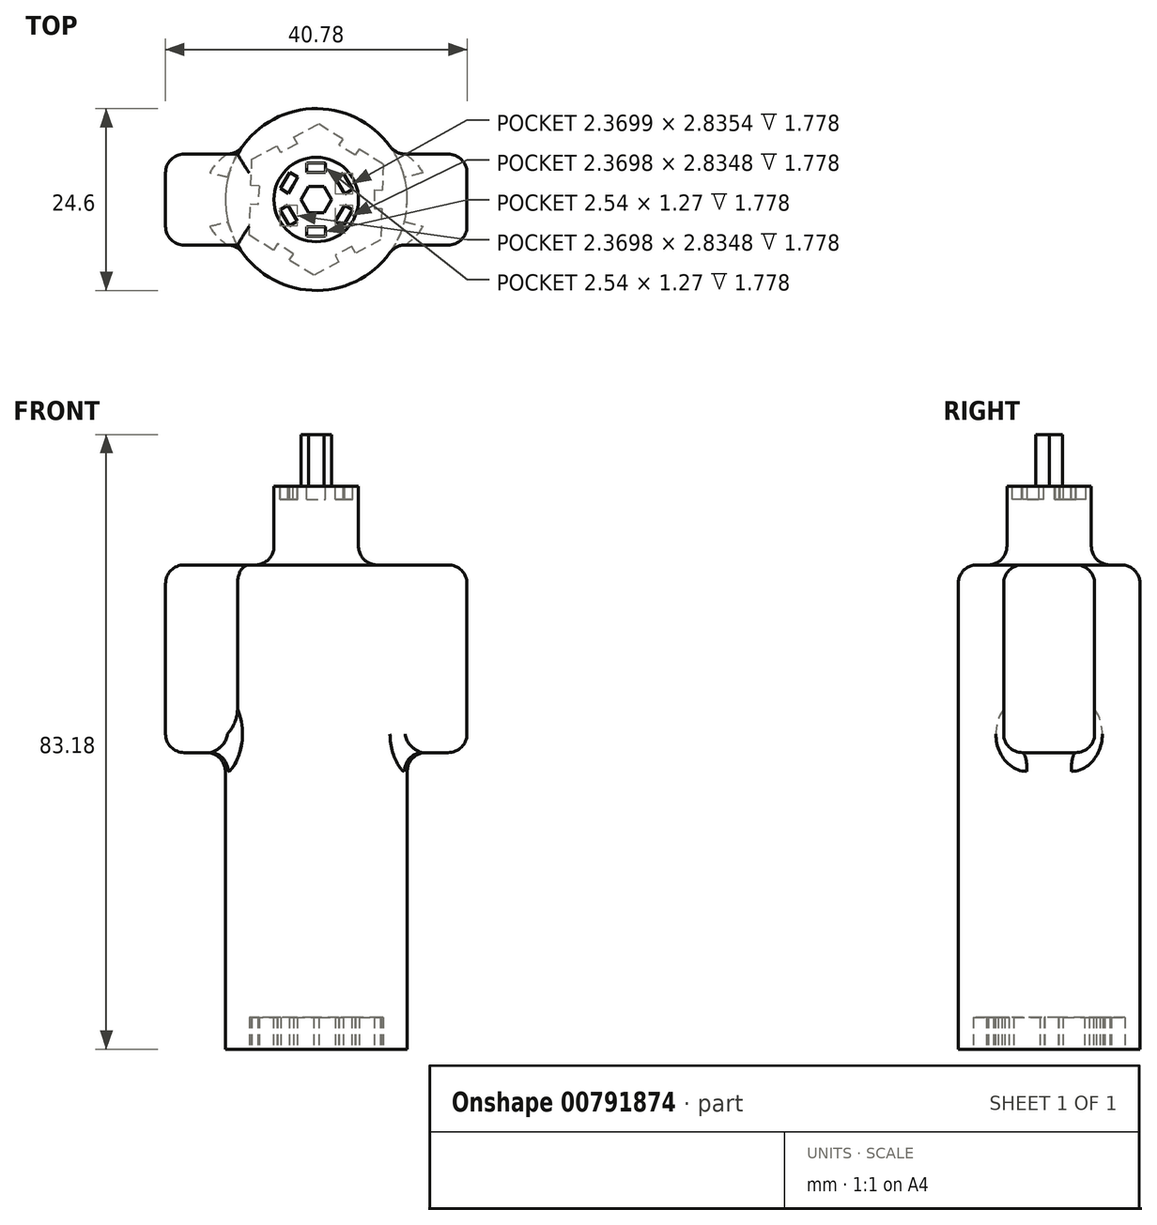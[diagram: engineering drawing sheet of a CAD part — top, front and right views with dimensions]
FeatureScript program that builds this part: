
annotation { "Feature Type Name" : "Feature", "Feature Type Description" : "" }
export const myFeature = defineFeature(function(context is Context, id is Id, definition is map)
    precondition{}
    {
        {
            var Q0;
            Q0=qCreatedBy(makeId("Top.planeOp"),FACE);
            var sketch = newSketch(context, id + "F0", { "sketchPlane" : qUnion([Q0])});
            skCircle(sketch, "E0.cCircle", {"center": v(0, 0) * mm, "radius": 8.9 * mm, "construction": true});
            skLineSegment(sketch, "E0.0", {"start": v(0.36, 10.26) * mm, "end": v(3.63, 8.21) * mm});
            skLineSegment(sketch, "E0.1", {"start": v(9.06, 4.82) * mm, "end": v(8.94, 1.27) * mm});
            skLineSegment(sketch, "E0.2", {"start": v(8.7, -5.44) * mm, "end": v(5.3, -7.25) * mm});
            skLineSegment(sketch, "E0.3", {"start": v(-0.36, -10.26) * mm, "end": v(-3.63, -8.21) * mm});
            skLineSegment(sketch, "E0.4", {"start": v(-9.06, -4.82) * mm, "end": v(-8.92, -0.61) * mm});
            skLineSegment(sketch, "E0.5", {"start": v(-8.7, 5.44) * mm, "end": v(-5.3, 7.25) * mm});
            skPoint(sketch, "E0.0.midPoint", {"position": v(4.71, 7.54) * mm});
            skLineSegment(sketch, "E1", {"start": v(0.36, 10.26) * mm, "end": v(-0.36, -10.26) * mm});
            skLineSegment(sketch, "E2", {"start": v(-9.06, -4.82) * mm, "end": v(9.06, 4.82) * mm});
            skLineSegment(sketch, "E3", {"start": v(-8.7, 5.44) * mm, "end": v(8.7, -5.44) * mm});
            skLineSegment(sketch, "E4", {"start": v(-3.05, 8.45) * mm, "end": v(-2.57, 7.55) * mm});
            skLineSegment(sketch, "E5", {"start": v(-2.57, 7.55) * mm, "end": v(-4.82, 6.36) * mm});
            skLineSegment(sketch, "E6", {"start": v(-4.82, 6.36) * mm, "end": v(-5.3, 7.25) * mm});
            skLineSegment(sketch, "E7.trimOffspring", {"start": v(-3.05, 8.45) * mm, "end": v(0.36, 10.26) * mm});
            skLineSegment(sketch, "E8.MirrorCS", {"start": v(2.57, -7.55) * mm, "end": v(3.05, -8.45) * mm});
            skLineSegment(sketch, "E9.MirrorCS", {"start": v(4.82, -6.36) * mm, "end": v(2.57, -7.55) * mm});
            skLineSegment(sketch, "E10.MirrorCS", {"start": v(5.3, -7.25) * mm, "end": v(4.82, -6.36) * mm});
            skLineSegment(sketch, "E11", {"start": v(5.79, 6.87) * mm, "end": v(5.25, 6) * mm});
            skLineSegment(sketch, "E12", {"start": v(5.25, 6) * mm, "end": v(3.1, 7.35) * mm});
            skLineSegment(sketch, "E13", {"start": v(3.1, 7.35) * mm, "end": v(3.63, 8.21) * mm});
            skLineSegment(sketch, "E14", {"start": v(7.84, 1.3) * mm, "end": v(7.84, -1.24) * mm});
            skLineSegment(sketch, "E15", {"start": v(7.84, -1.24) * mm, "end": v(8.85, -1.24) * mm});
            skLineSegment(sketch, "E16", {"start": v(7.84, 1.3) * mm, "end": v(8.94, 1.27) * mm});
            skLineSegment(sketch, "E17.MirrorCS", {"start": v(-3.1, -7.35) * mm, "end": v(-5.25, -6) * mm});
            skLineSegment(sketch, "E18.MirrorCS", {"start": v(-5.25, -6) * mm, "end": v(-5.79, -6.87) * mm});
            skLineSegment(sketch, "E19.MirrorCS", {"start": v(-3.63, -8.21) * mm, "end": v(-3.1, -7.35) * mm});
            skLineSegment(sketch, "E20.MirrorCS", {"start": v(-7.73, 1.85) * mm, "end": v(-8.83, 1.9) * mm});
            skLineSegment(sketch, "E21.MirrorCS", {"start": v(-7.73, 1.85) * mm, "end": v(-7.9, -0.68) * mm});
            skLineSegment(sketch, "E22.MirrorCS", {"start": v(-7.9, -0.68) * mm, "end": v(-8.92, -0.61) * mm});
            skLineSegment(sketch, "E23.trimOffspring", {"start": v(5.79, 6.87) * mm, "end": v(9.06, 4.82) * mm});
            skPoint(sketch, "E24.start.orphan", {"position": v(8.9, 0) * mm});
            skLineSegment(sketch, "E25.trimOffspring", {"start": v(8.85, -1.24) * mm, "end": v(8.7, -5.44) * mm});
            skLineSegment(sketch, "E26.trimOffspring", {"start": v(3.05, -8.45) * mm, "end": v(-0.36, -10.26) * mm});
            skLineSegment(sketch, "E27.trimOffspring", {"start": v(-5.79, -6.87) * mm, "end": v(-9.06, -4.82) * mm});
            skLineSegment(sketch, "E28.trimOffspring", {"start": v(-8.83, 1.9) * mm, "end": v(-8.7, 5.44) * mm});
            skPoint(sketch, "E29.start.orphan", {"position": v(-4.17, 7.85) * mm});
            skLineSegment(sketch, "E30", {"start": v(-5.3, 7.25) * mm, "end": v(-3.05, 8.45) * mm});
            skLineSegment(sketch, "E31", {"start": v(3.63, 8.21) * mm, "end": v(5.79, 6.87) * mm});
            skLineSegment(sketch, "E32", {"start": v(8.94, 1.27) * mm, "end": v(8.85, -1.24) * mm});
            skLineSegment(sketch, "E33", {"start": v(5.3, -7.25) * mm, "end": v(3.05, -8.45) * mm});
            skLineSegment(sketch, "E34", {"start": v(-5.79, -6.87) * mm, "end": v(-3.63, -8.21) * mm});
            skLineSegment(sketch, "E35", {"start": v(-8.83, 1.9) * mm, "end": v(-8.92, -0.61) * mm});
            skCircle(sketch, "E36", {"center": v(0, 0) * mm, "radius": 12.3 * mm});
            skSolve(sketch);
        }
        {
            var Q0;
            Q0=makeQuery(id+"F0.imprint","IMPRINT",FACE,{"disambiguationData":[TD([[makeQuery(id+"F0.imprint","IMPRINT",EDGE,{"derivedFrom":sQuery(id+"F0.wireOp",EDGE,"E0.0")}),1.0]])]});
            var Q1;
            Q1=makeQuery(id+"F0.imprint","IMPRINT",FACE,{"disambiguationData":[TD([[makeQuery(id+"F0.imprint","IMPRINT",EDGE,{"derivedFrom":sQuery(id+"F0.wireOp",EDGE,"E4")}),-1.0]])]});
            var Q2;
            Q2=makeQuery(id+"F0.imprint","IMPRINT",FACE,{"disambiguationData":[TD([[makeQuery(id+"F0.imprint","IMPRINT",EDGE,{"derivedFrom":sQuery(id+"F0.wireOp",EDGE,"E20.MirrorCS")}),1.0]])]});
            var Q3;
            Q3=makeQuery(id+"F0.imprint","IMPRINT",FACE,{"disambiguationData":[TD([[makeQuery(id+"F0.imprint","IMPRINT",EDGE,{"derivedFrom":sQuery(id+"F0.wireOp",EDGE,"E17.MirrorCS")}),1.0]])]});
            var Q4;
            Q4=makeQuery(id+"F0.imprint","IMPRINT",FACE,{"disambiguationData":[TD([[makeQuery(id+"F0.imprint","IMPRINT",EDGE,{"derivedFrom":sQuery(id+"F0.wireOp",EDGE,"E11")}),-1.0]])]});
            var Q5;
            {var subQ4=sQuery(id+"F0.wireOp",EDGE,"E0.0");Q5=makeQuery(id+"F0.imprint","IMPRINT",FACE,{"disambiguationData":[TD([[makeQuery(id+"F0.imprint","IMPRINT",EDGE,{"derivedFrom":subQ4}),-1.0]])]});}
            var Q6;
            {var subQ1=sQuery(id+"F0.wireOp",EDGE,"E0.5");Q6=makeQuery(id+"F0.imprint","IMPRINT",FACE,{"disambiguationData":[TD([[makeQuery(id+"F0.imprint","IMPRINT",EDGE,{"derivedFrom":subQ1}),-1.0]])]});}
            var Q7;
            {var subQ4=sQuery(id+"F0.wireOp",EDGE,"E0.4");Q7=makeQuery(id+"F0.imprint","IMPRINT",FACE,{"disambiguationData":[TD([[makeQuery(id+"F0.imprint","IMPRINT",EDGE,{"derivedFrom":subQ4}),-1.0]])]});}
            var Q8;
            {var subQ4=sQuery(id+"F0.wireOp",EDGE,"E0.1");Q8=makeQuery(id+"F0.imprint","IMPRINT",FACE,{"disambiguationData":[TD([[makeQuery(id+"F0.imprint","IMPRINT",EDGE,{"derivedFrom":subQ4}),-1.0]])]});}
            var Q9;
            Q9=makeQuery(id+"F0.imprint","IMPRINT",FACE,{"disambiguationData":[TD([[makeQuery(id+"F0.imprint","IMPRINT",EDGE,{"derivedFrom":sQuery(id+"F0.wireOp",EDGE,"E14")}),1.0]])]});
            var Q10;
            {var subQ1=sQuery(id+"F0.wireOp",EDGE,"E0.2");Q10=makeQuery(id+"F0.imprint","IMPRINT",FACE,{"disambiguationData":[TD([[makeQuery(id+"F0.imprint","IMPRINT",EDGE,{"derivedFrom":subQ1}),-1.0]])]});}
            var Q11;
            {var subQ0=sQuery(id+"F0.wireOp",EDGE,"E0.3");Q11=makeQuery(id+"F0.imprint","IMPRINT",FACE,{"disambiguationData":[TD([[makeQuery(id+"F0.imprint","IMPRINT",EDGE,{"derivedFrom":subQ0}),-1.0]])]});}
            var Q12;
            Q12=makeQuery(id+"F0.imprint","IMPRINT",FACE,{"disambiguationData":[TD([[makeQuery(id+"F0.imprint","IMPRINT",EDGE,{"derivedFrom":sQuery(id+"F0.wireOp",EDGE,"E8.MirrorCS")}),1.0]])]});
            extrude(context, id + "F1", {"entities" : qUnion([Q0, Q1, Q2, Q3, Q4, Q5, Q6, Q7, Q8, Q9, Q10, Q11, Q12]), "depth" : 76.2 * mm, "offsetDistance" : 25.4 * mm});
        }
        {
            var Q0;
            {var subQ1=sQuery(id+"F0.wireOp",EDGE,"E0.5");Q0=makeQuery(id+"F0.imprint","IMPRINT",FACE,{"disambiguationData":[TD([[makeQuery(id+"F0.imprint","IMPRINT",EDGE,{"derivedFrom":subQ1}),-1.0]])]});}
            var Q1;
            {var subQ4=sQuery(id+"F0.wireOp",EDGE,"E0.4");Q1=makeQuery(id+"F0.imprint","IMPRINT",FACE,{"disambiguationData":[TD([[makeQuery(id+"F0.imprint","IMPRINT",EDGE,{"derivedFrom":subQ4}),-1.0]])]});}
            var Q2;
            {var subQ0=sQuery(id+"F0.wireOp",EDGE,"E0.3");Q2=makeQuery(id+"F0.imprint","IMPRINT",FACE,{"disambiguationData":[TD([[makeQuery(id+"F0.imprint","IMPRINT",EDGE,{"derivedFrom":subQ0}),-1.0]])]});}
            var Q3;
            {var subQ1=sQuery(id+"F0.wireOp",EDGE,"E0.2");Q3=makeQuery(id+"F0.imprint","IMPRINT",FACE,{"disambiguationData":[TD([[makeQuery(id+"F0.imprint","IMPRINT",EDGE,{"derivedFrom":subQ1}),-1.0]])]});}
            var Q4;
            {var subQ4=sQuery(id+"F0.wireOp",EDGE,"E0.1");Q4=makeQuery(id+"F0.imprint","IMPRINT",FACE,{"disambiguationData":[TD([[makeQuery(id+"F0.imprint","IMPRINT",EDGE,{"derivedFrom":subQ4}),-1.0]])]});}
            var Q5;
            {var subQ4=sQuery(id+"F0.wireOp",EDGE,"E0.0");Q5=makeQuery(id+"F0.imprint","IMPRINT",FACE,{"disambiguationData":[TD([[makeQuery(id+"F0.imprint","IMPRINT",EDGE,{"derivedFrom":subQ4}),-1.0]])]});}
            extrude(context, id + "F2", {"entities" : qUnion([Q0, Q1, Q2, Q3, Q4, Q5]), "operationType" : NewBodyOperationType.REMOVE, "depth" : 4.32 * mm, "offsetDistance" : 25.4 * mm});
        }
        {
            var Q0;
            Q0=makeQuery(id+"F1.opExtrude","CAP_FACE",FACE,{"disambiguationData":[OSD([sQuery(id+"F0.wireOp",EDGE,"E36")])],"isStart":false});
            var sketch = newSketch(context, id + "F3", { "sketchPlane" : qUnion([Q0])});
            skCircle(sketch, "E37.cCircle", {"center": v(0, 0) * mm, "radius": 1.78 * mm, "construction": true});
            skLineSegment(sketch, "E37.0", {"start": v(-1.03, 1.78) * mm, "end": v(1.03, 1.78) * mm});
            skLineSegment(sketch, "E37.1", {"start": v(1.03, 1.78) * mm, "end": v(2.05, 0) * mm});
            skLineSegment(sketch, "E37.2", {"start": v(2.05, 0) * mm, "end": v(1.03, -1.78) * mm});
            skLineSegment(sketch, "E37.3", {"start": v(1.03, -1.78) * mm, "end": v(-1.03, -1.78) * mm});
            skLineSegment(sketch, "E37.4", {"start": v(-1.03, -1.78) * mm, "end": v(-2.05, 0) * mm});
            skLineSegment(sketch, "E37.5", {"start": v(-2.05, 0) * mm, "end": v(-1.03, 1.78) * mm});
            skPoint(sketch, "E37.0.midPoint", {"position": v(0, 1.78) * mm});
            skLineSegment(sketch, "E38.bottom", {"start": v(-1.27, 4.95) * mm, "end": v(1.27, 4.95) * mm});
            skLineSegment(sketch, "E38.top", {"start": v(-1.27, 3.68) * mm, "end": v(1.27, 3.68) * mm});
            skLineSegment(sketch, "E38.left", {"start": v(-1.27, 4.95) * mm, "end": v(-1.27, 3.68) * mm});
            skLineSegment(sketch, "E38.right", {"start": v(1.27, 4.95) * mm, "end": v(1.27, 3.68) * mm});
            skLineSegment(sketch, "E39", {"start": v(0, 4.95) * mm, "end": v(0, 0) * mm});
            skPoint(sketch, "E40.endSnap0", {"position": v(0, -1.78) * mm});
            skLineSegment(sketch, "E41", {"start": v(3.19, 1.84) * mm, "end": v(2.55, 2.94) * mm});
            skLineSegment(sketch, "E42", {"start": v(3.19, 1.84) * mm, "end": v(3.82, 0.74) * mm});
            skLineSegment(sketch, "E43", {"start": v(0, -3.68) * mm, "end": v(1.27, -3.68) * mm});
            skLineSegment(sketch, "E44", {"start": v(0, -3.68) * mm, "end": v(-1.27, -3.68) * mm});
            skLineSegment(sketch, "E45", {"start": v(-3.19, -1.84) * mm, "end": v(-2.55, -2.94) * mm});
            skLineSegment(sketch, "E46", {"start": v(-3.19, -1.84) * mm, "end": v(-3.82, -0.74) * mm});
            skLineSegment(sketch, "E47", {"start": v(-3.12, 1.93) * mm, "end": v(-2.48, 3.03) * mm});
            skLineSegment(sketch, "E48", {"start": v(-2.48, 3.03) * mm, "end": v(-3.58, 3.66) * mm});
            skLineSegment(sketch, "E49", {"start": v(2.55, 2.94) * mm, "end": v(2.56, 2.94) * mm});
            skLineSegment(sketch, "E50", {"start": v(3.82, 0.74) * mm, "end": v(4.92, 1.38) * mm});
            skLineSegment(sketch, "E51", {"start": v(1.27, -3.68) * mm, "end": v(1.27, -4.95) * mm});
            skLineSegment(sketch, "E52", {"start": v(-1.27, -3.68) * mm, "end": v(-1.27, -4.95) * mm});
            skLineSegment(sketch, "E53", {"start": v(-2.55, -2.94) * mm, "end": v(-3.65, -3.58) * mm});
            skPoint(sketch, "E54.endSnap0", {"position": v(-3.5, -1.3) * mm});
            skLineSegment(sketch, "E55", {"start": v(-3.12, 1.93) * mm, "end": v(-3.78, 0.85) * mm});
            skLineSegment(sketch, "E56", {"start": v(-3.78, 0.85) * mm, "end": v(-4.86, 1.51) * mm});
            skLineSegment(sketch, "E57", {"start": v(-4.86, 1.51) * mm, "end": v(-3.58, 3.66) * mm});
            skLineSegment(sketch, "E58", {"start": v(2.56, 2.94) * mm, "end": v(3.65, 3.58) * mm});
            skLineSegment(sketch, "E59", {"start": v(3.65, 3.58) * mm, "end": v(4.92, 1.38) * mm});
            skLineSegment(sketch, "E60", {"start": v(1.27, -4.95) * mm, "end": v(-1.27, -4.95) * mm});
            skLineSegment(sketch, "E61", {"start": v(-3.82, -0.74) * mm, "end": v(-4.92, -1.38) * mm});
            skLineSegment(sketch, "E62", {"start": v(-4.92, -1.38) * mm, "end": v(-3.65, -3.58) * mm});
            skLineSegment(sketch, "E63", {"start": v(-4.22, 2.59) * mm, "end": v(0, 0) * mm});
            skLineSegment(sketch, "E64", {"start": v(-4.29, -2.48) * mm, "end": v(0, 0) * mm});
            skLineSegment(sketch, "E65", {"start": v(4.29, 2.48) * mm, "end": v(0, 0) * mm});
            skLineSegment(sketch, "E66", {"start": v(0, -4.95) * mm, "end": v(0, 0) * mm});
            skLineSegment(sketch, "E67", {"start": v(-1.27, -4.95) * mm, "end": v(1.27, -4.95) * mm});
            skLineSegment(sketch, "E68", {"start": v(3.19, -1.84) * mm, "end": v(3.82, -0.74) * mm});
            skLineSegment(sketch, "E69", {"start": v(3.19, -1.84) * mm, "end": v(2.55, -2.94) * mm});
            skLineSegment(sketch, "E70", {"start": v(2.55, -2.94) * mm, "end": v(3.65, -3.58) * mm});
            skLineSegment(sketch, "E71", {"start": v(3.82, -0.74) * mm, "end": v(4.92, -1.38) * mm});
            skLineSegment(sketch, "E72", {"start": v(4.92, -1.38) * mm, "end": v(3.65, -3.58) * mm});
            skLineSegment(sketch, "E73", {"start": v(4.29, -2.48) * mm, "end": v(0, 0) * mm});
            skCircle(sketch, "E74", {"center": v(0, 0) * mm, "radius": 5.72 * mm});
            skCircle(sketch, "E75", {"center": v(0, 0) * mm, "radius": 12.63 * mm});
            skSolve(sketch);
        }
        {
            var Q0;
            {var subQ0=sQuery(id+"F3.wireOp",EDGE,"E37.1");var subQ1=sQuery(id+"F3.wireOp",EDGE,"E37.0");var subQ2=makeQuery(id+"F3.imprint","INTERSECT",VERTEX,{"derivedFrom":[subQ1,subQ0]});Q0=makeQuery(id+"F3.imprint","IMPRINT",FACE,{"disambiguationData":[TD([[makeQuery(id+"F3.imprint","IMPRINT",EDGE,{"disambiguationData":[TD([[subQ2,1.0]])],"derivedFrom":subQ1}),-1.0]])]});}
            var Q1;
            {var subQ0=sQuery(id+"F3.wireOp",EDGE,"E37.5");var subQ1=sQuery(id+"F3.wireOp",EDGE,"E37.0");var subQ2=makeQuery(id+"F3.imprint","INTERSECT",VERTEX,{"derivedFrom":[subQ1,subQ0]});Q1=makeQuery(id+"F3.imprint","IMPRINT",FACE,{"disambiguationData":[TD([[makeQuery(id+"F3.imprint","IMPRINT",EDGE,{"disambiguationData":[TD([[subQ2,-1.0]])],"derivedFrom":subQ1}),-1.0]])]});}
            var Q2;
            {var subQ0=sQuery(id+"F3.wireOp",EDGE,"E37.5");var subQ1=sQuery(id+"F3.wireOp",EDGE,"E37.4");var subQ2=makeQuery(id+"F3.imprint","INTERSECT",VERTEX,{"derivedFrom":[subQ1,subQ0]});Q2=makeQuery(id+"F3.imprint","IMPRINT",FACE,{"disambiguationData":[TD([[makeQuery(id+"F3.imprint","IMPRINT",EDGE,{"disambiguationData":[TD([[subQ2,1.0]])],"derivedFrom":subQ1}),-1.0]])]});}
            var Q3;
            {var subQ0=sQuery(id+"F3.wireOp",EDGE,"E37.4");var subQ1=sQuery(id+"F3.wireOp",EDGE,"E37.3");var subQ2=makeQuery(id+"F3.imprint","INTERSECT",VERTEX,{"derivedFrom":[subQ1,subQ0]});Q3=makeQuery(id+"F3.imprint","IMPRINT",FACE,{"disambiguationData":[TD([[makeQuery(id+"F3.imprint","IMPRINT",EDGE,{"disambiguationData":[TD([[subQ2,1.0]])],"derivedFrom":subQ1}),-1.0]])]});}
            var Q4;
            {var subQ0=sQuery(id+"F3.wireOp",EDGE,"E37.3");var subQ1=sQuery(id+"F3.wireOp",EDGE,"E37.2");var subQ2=makeQuery(id+"F3.imprint","INTERSECT",VERTEX,{"derivedFrom":[subQ1,subQ0]});Q4=makeQuery(id+"F3.imprint","IMPRINT",FACE,{"disambiguationData":[TD([[makeQuery(id+"F3.imprint","IMPRINT",EDGE,{"disambiguationData":[TD([[subQ2,1.0]])],"derivedFrom":subQ1}),-1.0]])]});}
            var Q5;
            {var subQ0=sQuery(id+"F3.wireOp",EDGE,"E37.2");var subQ1=sQuery(id+"F3.wireOp",EDGE,"E37.1");var subQ2=makeQuery(id+"F3.imprint","INTERSECT",VERTEX,{"derivedFrom":[subQ1,subQ0]});Q5=makeQuery(id+"F3.imprint","IMPRINT",FACE,{"disambiguationData":[TD([[makeQuery(id+"F3.imprint","IMPRINT",EDGE,{"disambiguationData":[TD([[subQ2,1.0]])],"derivedFrom":subQ1}),-1.0]])]});}
            extrude(context, id + "F4", {"entities" : qUnion([Q0, Q1, Q2, Q3, Q4, Q5]), "operationType" : NewBodyOperationType.ADD, "depth" : 6.98 * mm, "offsetDistance" : 25.4 * mm});
        }
        {
            var Q0;
            {var subQ0=sQuery(id+"F3.wireOp",EDGE,"E38.left");Q0=makeQuery(id+"F3.imprint","IMPRINT",FACE,{"disambiguationData":[TD([[makeQuery(id+"F3.imprint","IMPRINT",EDGE,{"derivedFrom":subQ0}),1.0]])]});}
            var Q1;
            {var subQ0=sQuery(id+"F3.wireOp",EDGE,"E38.right");Q1=makeQuery(id+"F3.imprint","IMPRINT",FACE,{"disambiguationData":[TD([[makeQuery(id+"F3.imprint","IMPRINT",EDGE,{"derivedFrom":subQ0}),-1.0]])]});}
            var Q2;
            {var subQ4=sQuery(id+"F3.wireOp",EDGE,"E41");Q2=makeQuery(id+"F3.imprint","IMPRINT",FACE,{"disambiguationData":[TD([[makeQuery(id+"F3.imprint","IMPRINT",EDGE,{"derivedFrom":subQ4}),-1.0]])]});}
            var Q3;
            {var subQ0=sQuery(id+"F3.wireOp",EDGE,"E42");Q3=makeQuery(id+"F3.imprint","IMPRINT",FACE,{"disambiguationData":[TD([[makeQuery(id+"F3.imprint","IMPRINT",EDGE,{"derivedFrom":subQ0}),1.0]])]});}
            var Q4;
            {var subQ0=sQuery(id+"F3.wireOp",EDGE,"E68");Q4=makeQuery(id+"F3.imprint","IMPRINT",FACE,{"disambiguationData":[TD([[makeQuery(id+"F3.imprint","IMPRINT",EDGE,{"derivedFrom":subQ0}),-1.0]])]});}
            var Q5;
            {var subQ0=sQuery(id+"F3.wireOp",EDGE,"E69");Q5=makeQuery(id+"F3.imprint","IMPRINT",FACE,{"disambiguationData":[TD([[makeQuery(id+"F3.imprint","IMPRINT",EDGE,{"derivedFrom":subQ0}),1.0]])]});}
            var Q6;
            {var subQ0=sQuery(id+"F3.wireOp",EDGE,"E43");Q6=makeQuery(id+"F3.imprint","IMPRINT",FACE,{"disambiguationData":[TD([[makeQuery(id+"F3.imprint","IMPRINT",EDGE,{"derivedFrom":subQ0}),-1.0]])]});}
            var Q7;
            {var subQ0=sQuery(id+"F3.wireOp",EDGE,"E44");Q7=makeQuery(id+"F3.imprint","IMPRINT",FACE,{"disambiguationData":[TD([[makeQuery(id+"F3.imprint","IMPRINT",EDGE,{"derivedFrom":subQ0}),1.0]])]});}
            var Q8;
            {var subQ0=sQuery(id+"F3.wireOp",EDGE,"E45");Q8=makeQuery(id+"F3.imprint","IMPRINT",FACE,{"disambiguationData":[TD([[makeQuery(id+"F3.imprint","IMPRINT",EDGE,{"derivedFrom":subQ0}),-1.0]])]});}
            var Q9;
            {var subQ0=sQuery(id+"F3.wireOp",EDGE,"E46");Q9=makeQuery(id+"F3.imprint","IMPRINT",FACE,{"disambiguationData":[TD([[makeQuery(id+"F3.imprint","IMPRINT",EDGE,{"derivedFrom":subQ0}),1.0]])]});}
            var Q10;
            {var subQ1=sQuery(id+"F3.wireOp",EDGE,"E47");Q10=makeQuery(id+"F3.imprint","IMPRINT",FACE,{"disambiguationData":[TD([[makeQuery(id+"F3.imprint","IMPRINT",EDGE,{"derivedFrom":subQ1}),1.0]])]});}
            var Q11;
            {var subQ3=sQuery(id+"F3.wireOp",EDGE,"E56");Q11=makeQuery(id+"F3.imprint","IMPRINT",FACE,{"disambiguationData":[TD([[makeQuery(id+"F3.imprint","IMPRINT",EDGE,{"derivedFrom":subQ3}),-1.0]])]});}
            extrude(context, id + "F5", {"entities" : qUnion([Q0, Q1, Q2, Q3, Q4, Q5, Q6, Q7, Q8, Q9, Q10, Q11]), "operationType" : NewBodyOperationType.REMOVE, "oppositeDirection" : true, "depth" : 1.78 * mm, "offsetDistance" : 25.4 * mm});
        }
        {
            var Q0;
            Q0=makeQuery(id+"F3.imprint","IMPRINT",FACE,{"disambiguationData":[TD([[makeQuery(id+"F3.imprint","IMPRINT",EDGE,{"derivedFrom":sQuery(id+"F3.wireOp",EDGE,"E74")}),-1.0]])]});
            extrude(context, id + "F6", {"entities" : qUnion([Q0]), "operationType" : NewBodyOperationType.REMOVE, "oppositeDirection" : true, "depth" : 10.67 * mm, "offsetDistance" : 25.4 * mm});
        }
        {
            var Q0;
            Q0=makeQuery(id+"F6.boolean.opBoolean","COPY",FACE,{"derivedFrom":makeQuery(id+"F6.opExtrude","CAP_FACE",FACE,{"disambiguationData":[OSD([sQuery(id+"F0.wireOp",EDGE,"E36"),sQuery(id+"F3.wireOp",EDGE,"E74")])],"isStart":false})});
            var sketch = newSketch(context, id + "F7", { "sketchPlane" : qUnion([Q0])});
            skLineSegment(sketch, "E76.bottom", {"start": v(-10.66, 6.15) * mm, "end": v(-20.39, 6.15) * mm});
            skLineSegment(sketch, "E76.top", {"start": v(-10.66, -6.15) * mm, "end": v(-20.39, -6.15) * mm});
            skLineSegment(sketch, "E76.left", {"start": v(-10.66, 6.15) * mm, "end": v(-10.66, -6.15) * mm});
            skLineSegment(sketch, "E76.right", {"start": v(-20.39, 6.15) * mm, "end": v(-20.39, -6.15) * mm});
            skLineSegment(sketch, "E77", {"start": v(0, 12.3) * mm, "end": v(0, -12.3) * mm});
            skLineSegment(sketch, "E78.MirrorCS", {"start": v(10.66, 6.15) * mm, "end": v(20.39, 6.15) * mm});
            skLineSegment(sketch, "E79.MirrorCS", {"start": v(20.39, 6.15) * mm, "end": v(20.39, -6.15) * mm});
            skLineSegment(sketch, "E80.MirrorCS", {"start": v(10.66, -6.15) * mm, "end": v(20.39, -6.15) * mm});
            skLineSegment(sketch, "E81.MirrorCS", {"start": v(10.66, 6.15) * mm, "end": v(10.66, -6.15) * mm});
            skPoint(sketch, "E82.MirrorCS.end.orphan", {"position": v(-20.39, 18.45) * mm});
            skPoint(sketch, "E82.MirrorCS.start.orphan", {"position": v(-20.39, 6.15) * mm});
            skLineSegment(sketch, "E83", {"start": v(0, 0) * mm, "end": v(-20.39, 0) * mm});
            skLineSegment(sketch, "E84", {"start": v(0, 0) * mm, "end": v(20.39, 0) * mm});
            skSolve(sketch);
        }
        {
            var Q0;
            {var subQ0=sQuery(id+"F7.wireOp",EDGE,"E76.bottom");Q0=makeQuery(id+"F7.imprint","IMPRINT",FACE,{"disambiguationData":[TD([[makeQuery(id+"F7.imprint","IMPRINT",EDGE,{"derivedFrom":subQ0}),1.0]])]});}
            var Q1;
            {var subQ0=sQuery(id+"F7.wireOp",EDGE,"E78.MirrorCS");Q1=makeQuery(id+"F7.imprint","IMPRINT",FACE,{"disambiguationData":[TD([[makeQuery(id+"F7.imprint","IMPRINT",EDGE,{"derivedFrom":subQ0}),-1.0]])]});}
            var Q2;
            {var subQ0=sQuery(id+"F7.wireOp",EDGE,"E76.top");Q2=makeQuery(id+"F7.imprint","IMPRINT",FACE,{"disambiguationData":[TD([[makeQuery(id+"F7.imprint","IMPRINT",EDGE,{"derivedFrom":subQ0}),-1.0]])]});}
            var Q3;
            {var subQ0=sQuery(id+"F7.wireOp",EDGE,"E80.MirrorCS");Q3=makeQuery(id+"F7.imprint","IMPRINT",FACE,{"disambiguationData":[TD([[makeQuery(id+"F7.imprint","IMPRINT",EDGE,{"derivedFrom":subQ0}),1.0]])]});}
            extrude(context, id + "F8", {"entities" : qUnion([Q0, Q1, Q2, Q3]), "operationType" : NewBodyOperationType.ADD, "oppositeDirection" : true, "depth" : 25.4 * mm, "offsetDistance" : 25.4 * mm});
        }
        {
            var Q0;
            Q0=makeQuery(id+"F8.opExtrude","SWEPT_FACE",FACE,{"disambiguationData":[OSD([sQuery(id+"F7.wireOp",EDGE,"E76.right")])]});
            var Q1;
            Q1=makeQuery(id+"F8.opExtrude","CAP_FACE",FACE,{"disambiguationData":[OSD([sQuery(id+"F0.wireOp",EDGE,"E36"),sQuery(id+"F7.wireOp",EDGE,"E76.bottom"),sQuery(id+"F7.wireOp",EDGE,"E76.top"),sQuery(id+"F7.wireOp",EDGE,"E76.right")])],"isStart":false});
            var Q2;
            Q2=makeQuery(id+"F8.opExtrude","CAP_EDGE",EDGE,{"disambiguationData":[OSD([sQuery(id+"F7.wireOp",EDGE,"E76.top")])],"isStart":true});
            var Q3;
            Q3=makeQuery(id+"F8.opExtrude","CAP_EDGE",EDGE,{"disambiguationData":[OSD([sQuery(id+"F7.wireOp",EDGE,"E76.bottom")])],"isStart":true});
            var Q4;
            {var subQ0=sQuery(id+"F0.wireOp",EDGE,"E36");Q4=makeQuery(id+"F8.boolean.opBoolean","MERGE",FACE,{"derivedFrom":[makeQuery(id+"F6.boolean.opBoolean","COPY",FACE,{"derivedFrom":makeQuery(id+"F6.opExtrude","CAP_FACE",FACE,{"disambiguationData":[OSD([subQ0,sQuery(id+"F3.wireOp",EDGE,"E74")])],"isStart":false})}),makeQuery(id+"F8.opExtrude","CAP_FACE",FACE,{"disambiguationData":[OSD([subQ0,sQuery(id+"F7.wireOp",EDGE,"E76.bottom"),sQuery(id+"F7.wireOp",EDGE,"E76.top"),sQuery(id+"F7.wireOp",EDGE,"E76.right")])],"isStart":true}),makeQuery(id+"F8.opExtrude","CAP_FACE",FACE,{"disambiguationData":[OSD([subQ0,sQuery(id+"F7.wireOp",EDGE,"E78.MirrorCS"),sQuery(id+"F7.wireOp",EDGE,"E79.MirrorCS"),sQuery(id+"F7.wireOp",EDGE,"E80.MirrorCS")])],"isStart":true})]});}
            var Q5;
            Q5=makeQuery(id+"F8.opExtrude","SWEPT_FACE",FACE,{"disambiguationData":[OSD([sQuery(id+"F7.wireOp",EDGE,"E79.MirrorCS")])]});
            var Q6;
            Q6=makeQuery(id+"F8.opExtrude","SWEPT_FACE",FACE,{"disambiguationData":[OSD([sQuery(id+"F7.wireOp",EDGE,"E80.MirrorCS")])]});
            var Q7;
            Q7=makeQuery(id+"F8.opExtrude","SWEPT_FACE",FACE,{"disambiguationData":[OSD([sQuery(id+"F7.wireOp",EDGE,"E78.MirrorCS")])]});
            var Q8;
            Q8=makeQuery(id+"F8.opExtrude","CAP_FACE",FACE,{"disambiguationData":[OSD([sQuery(id+"F0.wireOp",EDGE,"E36"),sQuery(id+"F7.wireOp",EDGE,"E78.MirrorCS"),sQuery(id+"F7.wireOp",EDGE,"E79.MirrorCS"),sQuery(id+"F7.wireOp",EDGE,"E80.MirrorCS")])],"isStart":false});
            fillet(context, id + "F9", {"entities" : qUnion([Q0, Q1, Q2, Q3, Q4, Q5, Q6, Q7, Q8]), "tangentPropagation" : true, "radius" : 2.54 * mm, "defaultsChanged" : false, "vertexSettings" : [], "allowEdgeOverflow" : false});
        }
    });
